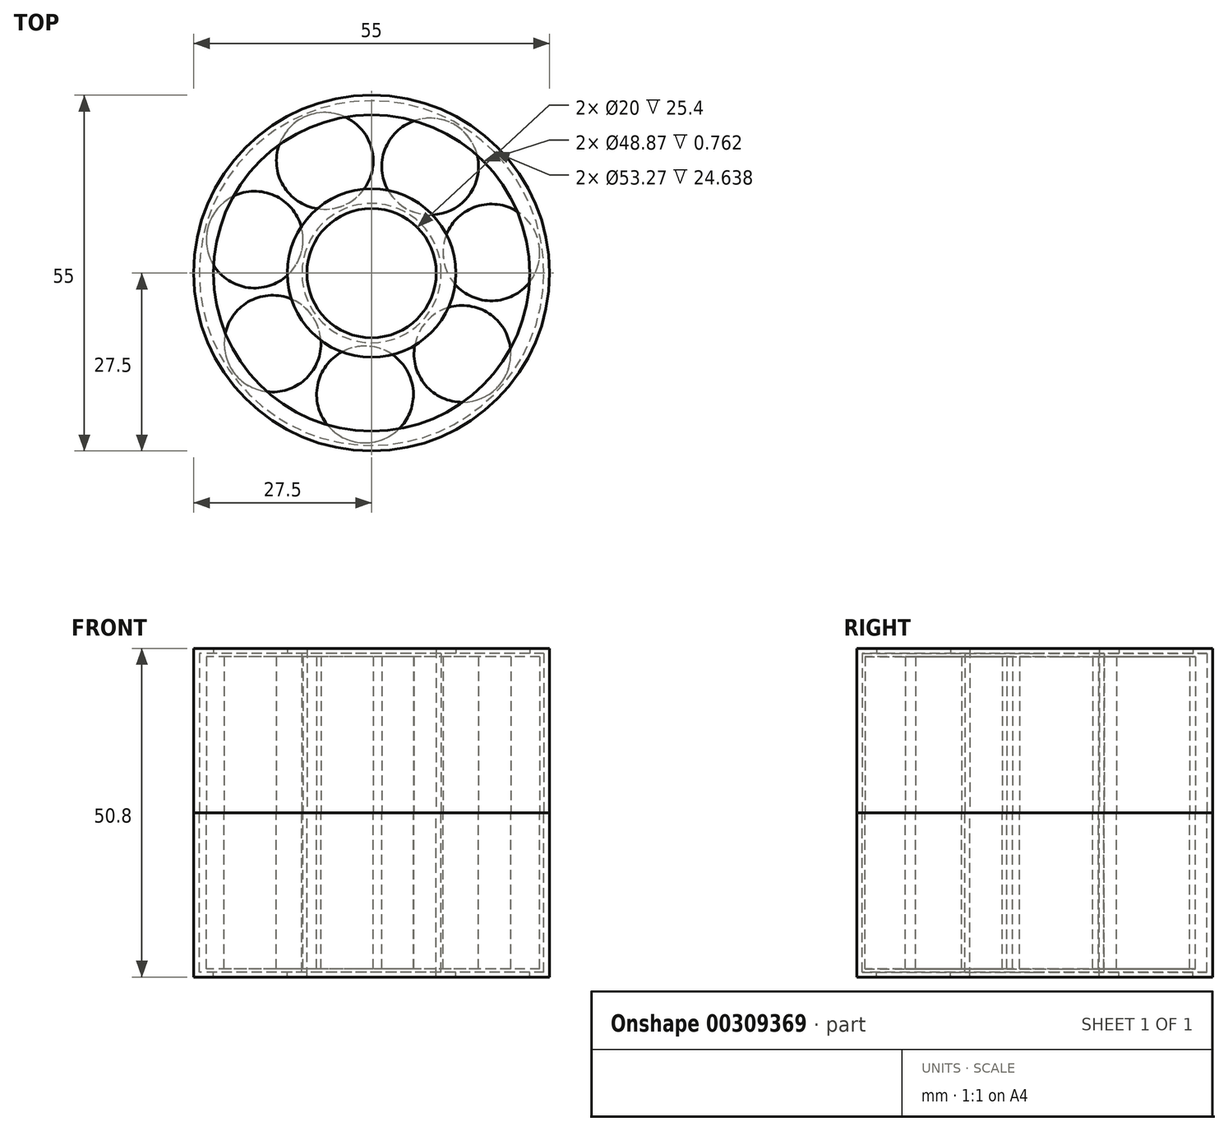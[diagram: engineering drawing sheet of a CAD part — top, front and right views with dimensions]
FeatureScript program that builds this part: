
annotation { "Feature Type Name" : "Feature", "Feature Type Description" : "" }
export const myFeature = defineFeature(function(context is Context, id is Id, definition is map)
    precondition{}
    {
        {
            var Q0;
            Q0=qCreatedBy(makeId("Top.planeOp"),FACE);
            var sketch = newSketch(context, id + "F0", { "sketchPlane" : qUnion([Q0])});
            skCircle(sketch, "E0", {"center": v(0, 0) * mm, "radius": 10 * mm});
            skCircle(sketch, "E1", {"center": v(0, 0) * mm, "radius": 27.5 * mm});
            skCircle(sketch, "E2", {"center": v(0, 0) * mm, "radius": 13.02 * mm});
            skCircle(sketch, "E3", {"center": v(0, 0) * mm, "radius": 24.43 * mm});
            skCircle(sketch, "E4", {"center": v(0, 0) * mm, "radius": 18.75 * mm, "construction": true});
            skCircle(sketch, "E5", {"center": v(0, 0) * mm, "radius": 10.76 * mm});
            skCircle(sketch, "E6", {"center": v(0, 0) * mm, "radius": 26.63 * mm});
            skCircle(sketch, "E7.cCircle", {"center": v(0, 0) * mm, "radius": 16.93 * mm, "construction": true});
            skLineSegment(sketch, "E7.0", {"start": v(9.05, 16.47) * mm, "end": v(18.52, 3.19) * mm});
            skLineSegment(sketch, "E7.1", {"start": v(18.52, 3.19) * mm, "end": v(14.04, -12.5) * mm});
            skLineSegment(sketch, "E7.2", {"start": v(14.04, -12.5) * mm, "end": v(-1.01, -18.76) * mm});
            skLineSegment(sketch, "E7.3", {"start": v(-1.01, -18.76) * mm, "end": v(-15.3, -10.9) * mm});
            skLineSegment(sketch, "E7.4", {"start": v(-15.3, -10.9) * mm, "end": v(-18.07, 5.16) * mm});
            skLineSegment(sketch, "E7.5", {"start": v(-18.07, 5.16) * mm, "end": v(-7.23, 17.34) * mm});
            skLineSegment(sketch, "E7.6", {"start": v(-7.23, 17.34) * mm, "end": v(9.05, 16.47) * mm});
            skPoint(sketch, "E7.0.midPoint", {"position": v(13.79, 9.83) * mm});
            skCircle(sketch, "E8", {"center": v(-7.23, 17.34) * mm, "radius": 7.48 * mm});
            skCircle(sketch, "E9", {"center": v(9.05, 16.47) * mm, "radius": 7.48 * mm});
            skCircle(sketch, "E10", {"center": v(18.52, 3.19) * mm, "radius": 7.48 * mm});
            skCircle(sketch, "E11", {"center": v(14.04, -12.5) * mm, "radius": 7.48 * mm});
            skCircle(sketch, "E12", {"center": v(-1.01, -18.76) * mm, "radius": 7.48 * mm});
            skCircle(sketch, "E13", {"center": v(-15.3, -10.9) * mm, "radius": 7.48 * mm});
            skCircle(sketch, "E14", {"center": v(-18.07, 5.16) * mm, "radius": 7.48 * mm});
            skSolve(sketch);
        }
        {
            var Q0;
            Q0 = qSketchRegion(id + "F0", true);
            var Q1;
            Q1=makeQuery(id+"F0.imprint","IMPRINT",FACE,{"disambiguationData":[TD([[makeQuery(id+"F0.imprint","IMPRINT",EDGE,{"derivedFrom":sQuery(id+"F0.wireOp",EDGE,"E0")}),-1.0]])]});
            var Q2;
            Q2=makeQuery(id+"F0.imprint","IMPRINT",FACE,{"disambiguationData":[TD([[makeQuery(id+"F0.imprint","IMPRINT",EDGE,{"derivedFrom":sQuery(id+"F0.wireOp",EDGE,"nIhnmfeC-0gWH-qgGF-FQwQ-DqKGUn8nxgKd")}),-1.0]])]});
            var Q3;
            Q3=makeQuery(id+"F0.imprint","IMPRINT",FACE,{"disambiguationData":[TD([[makeQuery(id+"F0.imprint","IMPRINT",EDGE,{"derivedFrom":sQuery(id+"F0.wireOp",EDGE,"kMlYBa3b-KAGz-d3cv-tEsV-yyaXbjt7PMGd")}),1.0]])]});
            var Q4;
            {var subQ0=sQuery(id+"F0.wireOp",EDGE,"E2");var subQ1=sQuery(id+"F0.wireOp",EDGE,"VeNGo6Cm-qSl3-L9k0-Q7Ts-Sp1q9LBLhO9i");var subQ2=makeQuery(id+"F0.imprint","INTERSECT",VERTEX,{"disambiguationData":[OD(0.0)],"derivedFrom":[subQ1,subQ0]});Q4=makeQuery(id+"F0.imprint","IMPRINT",FACE,{"disambiguationData":[TD([[makeQuery(id+"F0.imprint","IMPRINT",EDGE,{"disambiguationData":[TD([[subQ2,-1.0]])],"derivedFrom":subQ1}),1.0]])]});}
            var Q5;
            {var subQ0=sQuery(id+"F0.wireOp",EDGE,"E2");var subQ1=sQuery(id+"F0.wireOp",EDGE,"zqxHkr2o-9LMR-s23B-vHwf-xSVSSCzzs4RS");var subQ2=makeQuery(id+"F0.imprint","INTERSECT",VERTEX,{"disambiguationData":[OD(0.0)],"derivedFrom":[subQ1,subQ0]});Q5=makeQuery(id+"F0.imprint","IMPRINT",FACE,{"disambiguationData":[TD([[makeQuery(id+"F0.imprint","IMPRINT",EDGE,{"disambiguationData":[TD([[subQ2,1.0]])],"derivedFrom":subQ1}),1.0]])]});}
            var Q6;
            {var subQ0=sQuery(id+"F0.wireOp",EDGE,"E2");var subQ1=sQuery(id+"F0.wireOp",EDGE,"xxg3d6mS-jKbs-yPx6-TI2x-z0IN7hIOQDgV");var subQ2=makeQuery(id+"F0.imprint","INTERSECT",VERTEX,{"disambiguationData":[OD(0.0)],"derivedFrom":[subQ1,subQ0]});Q6=makeQuery(id+"F0.imprint","IMPRINT",FACE,{"disambiguationData":[TD([[makeQuery(id+"F0.imprint","IMPRINT",EDGE,{"disambiguationData":[TD([[subQ2,1.0]])],"derivedFrom":subQ1}),1.0]])]});}
            var Q7;
            {var subQ0=sQuery(id+"F0.wireOp",EDGE,"E2");var subQ1=sQuery(id+"F0.wireOp",EDGE,"EG8hidmS-nRKZ-wcGO-puJM-sy69pmvQp8kP");var subQ2=makeQuery(id+"F0.imprint","INTERSECT",VERTEX,{"disambiguationData":[OD(0.0)],"derivedFrom":[subQ1,subQ0]});Q7=makeQuery(id+"F0.imprint","IMPRINT",FACE,{"disambiguationData":[TD([[makeQuery(id+"F0.imprint","IMPRINT",EDGE,{"disambiguationData":[TD([[subQ2,-1.0]])],"derivedFrom":subQ1}),1.0]])]});}
            var Q8;
            {var subQ0=sQuery(id+"F0.wireOp",EDGE,"E2");var subQ1=sQuery(id+"F0.wireOp",EDGE,"lMHOxLXC-queE-13hP-3AmH-u1hImJZGGyEp");var subQ2=makeQuery(id+"F0.imprint","INTERSECT",VERTEX,{"disambiguationData":[OD(0.0)],"derivedFrom":[subQ1,subQ0]});Q8=makeQuery(id+"F0.imprint","IMPRINT",FACE,{"disambiguationData":[TD([[makeQuery(id+"F0.imprint","IMPRINT",EDGE,{"disambiguationData":[TD([[subQ2,-1.0]])],"derivedFrom":subQ1}),1.0]])]});}
            var Q9;
            {var subQ0=sQuery(id+"F0.wireOp",EDGE,"E2");var subQ1=sQuery(id+"F0.wireOp",EDGE,"Q5qxaiEa-uetU-TrzA-PZdv-cf9O0egGTCUz");var subQ2=makeQuery(id+"F0.imprint","INTERSECT",VERTEX,{"disambiguationData":[OD(0.0)],"derivedFrom":[subQ1,subQ0]});Q9=makeQuery(id+"F0.imprint","IMPRINT",FACE,{"disambiguationData":[TD([[makeQuery(id+"F0.imprint","IMPRINT",EDGE,{"disambiguationData":[TD([[subQ2,-1.0]])],"derivedFrom":subQ1}),1.0]])]});}
            var Q10;
            {var subQ0=sQuery(id+"F0.wireOp",EDGE,"np1IEidV-92wI-X2Ku-ilMX-xF02V59ttlWc");var subQ1=sQuery(id+"F0.wireOp",EDGE,"VeNGo6Cm-qSl3-L9k0-Q7Ts-Sp1q9LBLhO9i");var subQ2=makeQuery(id+"F0.imprint","INTERSECT",VERTEX,{"disambiguationData":[OD(0.0)],"derivedFrom":[subQ1,subQ0]});Q10=makeQuery(id+"F0.imprint","IMPRINT",FACE,{"disambiguationData":[TD([[makeQuery(id+"F0.imprint","IMPRINT",EDGE,{"disambiguationData":[TD([[subQ2,1.0]])],"derivedFrom":subQ1}),1.0]])]});}
            var Q11;
            {var subQ0=sQuery(id+"F0.wireOp",EDGE,"np1IEidV-92wI-X2Ku-ilMX-xF02V59ttlWc");var subQ1=sQuery(id+"F0.wireOp",EDGE,"Q5qxaiEa-uetU-TrzA-PZdv-cf9O0egGTCUz");var subQ2=makeQuery(id+"F0.imprint","INTERSECT",VERTEX,{"disambiguationData":[OD(0.0)],"derivedFrom":[subQ1,subQ0]});Q11=makeQuery(id+"F0.imprint","IMPRINT",FACE,{"disambiguationData":[TD([[makeQuery(id+"F0.imprint","IMPRINT",EDGE,{"disambiguationData":[TD([[subQ2,1.0]])],"derivedFrom":subQ1}),1.0]])]});}
            var Q12;
            {var subQ0=sQuery(id+"F0.wireOp",EDGE,"np1IEidV-92wI-X2Ku-ilMX-xF02V59ttlWc");var subQ1=sQuery(id+"F0.wireOp",EDGE,"lMHOxLXC-queE-13hP-3AmH-u1hImJZGGyEp");var subQ2=makeQuery(id+"F0.imprint","INTERSECT",VERTEX,{"disambiguationData":[OD(0.0)],"derivedFrom":[subQ1,subQ0]});Q12=makeQuery(id+"F0.imprint","IMPRINT",FACE,{"disambiguationData":[TD([[makeQuery(id+"F0.imprint","IMPRINT",EDGE,{"disambiguationData":[TD([[subQ2,1.0]])],"derivedFrom":subQ1}),1.0]])]});}
            var Q13;
            {var subQ0=sQuery(id+"F0.wireOp",EDGE,"np1IEidV-92wI-X2Ku-ilMX-xF02V59ttlWc");var subQ1=sQuery(id+"F0.wireOp",EDGE,"EG8hidmS-nRKZ-wcGO-puJM-sy69pmvQp8kP");var subQ2=makeQuery(id+"F0.imprint","INTERSECT",VERTEX,{"disambiguationData":[OD(0.0)],"derivedFrom":[subQ1,subQ0]});Q13=makeQuery(id+"F0.imprint","IMPRINT",FACE,{"disambiguationData":[TD([[makeQuery(id+"F0.imprint","IMPRINT",EDGE,{"disambiguationData":[TD([[subQ2,-1.0]])],"derivedFrom":subQ1}),1.0]])]});}
            var Q14;
            {var subQ0=sQuery(id+"F0.wireOp",EDGE,"np1IEidV-92wI-X2Ku-ilMX-xF02V59ttlWc");var subQ1=sQuery(id+"F0.wireOp",EDGE,"xxg3d6mS-jKbs-yPx6-TI2x-z0IN7hIOQDgV");var subQ2=makeQuery(id+"F0.imprint","INTERSECT",VERTEX,{"disambiguationData":[OD(0.0)],"derivedFrom":[subQ1,subQ0]});Q14=makeQuery(id+"F0.imprint","IMPRINT",FACE,{"disambiguationData":[TD([[makeQuery(id+"F0.imprint","IMPRINT",EDGE,{"disambiguationData":[TD([[subQ2,-1.0]])],"derivedFrom":subQ1}),1.0]])]});}
            var Q15;
            {var subQ0=sQuery(id+"F0.wireOp",EDGE,"np1IEidV-92wI-X2Ku-ilMX-xF02V59ttlWc");var subQ1=sQuery(id+"F0.wireOp",EDGE,"zqxHkr2o-9LMR-s23B-vHwf-xSVSSCzzs4RS");var subQ2=makeQuery(id+"F0.imprint","INTERSECT",VERTEX,{"disambiguationData":[OD(0.0)],"derivedFrom":[subQ1,subQ0]});Q15=makeQuery(id+"F0.imprint","IMPRINT",FACE,{"disambiguationData":[TD([[makeQuery(id+"F0.imprint","IMPRINT",EDGE,{"disambiguationData":[TD([[subQ2,-1.0]])],"derivedFrom":subQ1}),1.0]])]});}
            var Q16;
            Q16=makeQuery(id+"F0.imprint","IMPRINT",FACE,{"disambiguationData":[TD([[makeQuery(id+"F0.imprint","IMPRINT",EDGE,{"derivedFrom":sQuery(id+"F0.wireOp",EDGE,"E6")}),1.0]])]});
            var Q17;
            {var subQ0=sQuery(id+"F0.wireOp",EDGE,"E9");var subQ1=sQuery(id+"F0.wireOp",EDGE,"E3");var subQ2=makeQuery(id+"F0.imprint","INTERSECT",VERTEX,{"disambiguationData":[OD(0.0)],"derivedFrom":[subQ1,subQ0]});Q17=makeQuery(id+"F0.imprint","IMPRINT",FACE,{"disambiguationData":[TD([[makeQuery(id+"F0.imprint","IMPRINT",EDGE,{"disambiguationData":[TD([[subQ2,-1.0]])],"derivedFrom":subQ1}),-1.0]])]});}
            var Q18;
            {var subQ0=sQuery(id+"F0.wireOp",EDGE,"E10");var subQ1=sQuery(id+"F0.wireOp",EDGE,"E3");var subQ2=makeQuery(id+"F0.imprint","INTERSECT",VERTEX,{"disambiguationData":[OD(0.0)],"derivedFrom":[subQ1,subQ0]});Q18=makeQuery(id+"F0.imprint","IMPRINT",FACE,{"disambiguationData":[TD([[makeQuery(id+"F0.imprint","IMPRINT",EDGE,{"disambiguationData":[TD([[subQ2,1.0]])],"derivedFrom":subQ1}),-1.0]])]});}
            var Q19;
            {var subQ0=sQuery(id+"F0.wireOp",EDGE,"E11");var subQ1=sQuery(id+"F0.wireOp",EDGE,"E3");var subQ2=makeQuery(id+"F0.imprint","INTERSECT",VERTEX,{"disambiguationData":[OD(0.0)],"derivedFrom":[subQ1,subQ0]});Q19=makeQuery(id+"F0.imprint","IMPRINT",FACE,{"disambiguationData":[TD([[makeQuery(id+"F0.imprint","IMPRINT",EDGE,{"disambiguationData":[TD([[subQ2,-1.0]])],"derivedFrom":subQ1}),-1.0]])]});}
            var Q20;
            {var subQ0=sQuery(id+"F0.wireOp",EDGE,"E12");var subQ1=sQuery(id+"F0.wireOp",EDGE,"E3");var subQ2=makeQuery(id+"F0.imprint","INTERSECT",VERTEX,{"disambiguationData":[OD(0.0)],"derivedFrom":[subQ1,subQ0]});Q20=makeQuery(id+"F0.imprint","IMPRINT",FACE,{"disambiguationData":[TD([[makeQuery(id+"F0.imprint","IMPRINT",EDGE,{"disambiguationData":[TD([[subQ2,-1.0]])],"derivedFrom":subQ1}),-1.0]])]});}
            var Q21;
            {var subQ0=sQuery(id+"F0.wireOp",EDGE,"E13");var subQ1=sQuery(id+"F0.wireOp",EDGE,"E3");var subQ2=makeQuery(id+"F0.imprint","INTERSECT",VERTEX,{"disambiguationData":[OD(0.0)],"derivedFrom":[subQ1,subQ0]});Q21=makeQuery(id+"F0.imprint","IMPRINT",FACE,{"disambiguationData":[TD([[makeQuery(id+"F0.imprint","IMPRINT",EDGE,{"disambiguationData":[TD([[subQ2,-1.0]])],"derivedFrom":subQ1}),-1.0]])]});}
            var Q22;
            {var subQ0=sQuery(id+"F0.wireOp",EDGE,"E14");var subQ1=sQuery(id+"F0.wireOp",EDGE,"E3");var subQ2=makeQuery(id+"F0.imprint","INTERSECT",VERTEX,{"disambiguationData":[OD(0.0)],"derivedFrom":[subQ1,subQ0]});Q22=makeQuery(id+"F0.imprint","IMPRINT",FACE,{"disambiguationData":[TD([[makeQuery(id+"F0.imprint","IMPRINT",EDGE,{"disambiguationData":[TD([[subQ2,-1.0]])],"derivedFrom":subQ1}),-1.0]])]});}
            var Q23;
            {var subQ0=sQuery(id+"F0.wireOp",EDGE,"E8");var subQ1=sQuery(id+"F0.wireOp",EDGE,"E3");var subQ2=makeQuery(id+"F0.imprint","INTERSECT",VERTEX,{"disambiguationData":[OD(0.0)],"derivedFrom":[subQ1,subQ0]});Q23=makeQuery(id+"F0.imprint","IMPRINT",FACE,{"disambiguationData":[TD([[makeQuery(id+"F0.imprint","IMPRINT",EDGE,{"disambiguationData":[TD([[subQ2,-1.0]])],"derivedFrom":subQ1}),-1.0]])]});}
            var Q24;
            Q24=makeQuery(id+"F0.imprint","IMPRINT",FACE,{"disambiguationData":[TD([[makeQuery(id+"F0.imprint","IMPRINT",EDGE,{"derivedFrom":sQuery(id+"F0.wireOp",EDGE,"E5")}),-1.0]])]});
            var Q25;
            {var subQ0=sQuery(id+"F0.wireOp",EDGE,"E8");var subQ1=sQuery(id+"F0.wireOp",EDGE,"E2");var subQ2=makeQuery(id+"F0.imprint","INTERSECT",VERTEX,{"disambiguationData":[OD(0.0)],"derivedFrom":[subQ1,subQ0]});Q25=makeQuery(id+"F0.imprint","IMPRINT",FACE,{"disambiguationData":[TD([[makeQuery(id+"F0.imprint","IMPRINT",EDGE,{"disambiguationData":[TD([[subQ2,-1.0]])],"derivedFrom":subQ1}),1.0]])]});}
            var Q26;
            {var subQ0=sQuery(id+"F0.wireOp",EDGE,"E9");var subQ1=sQuery(id+"F0.wireOp",EDGE,"E2");var subQ2=makeQuery(id+"F0.imprint","INTERSECT",VERTEX,{"disambiguationData":[OD(0.0)],"derivedFrom":[subQ1,subQ0]});Q26=makeQuery(id+"F0.imprint","IMPRINT",FACE,{"disambiguationData":[TD([[makeQuery(id+"F0.imprint","IMPRINT",EDGE,{"disambiguationData":[TD([[subQ2,-1.0]])],"derivedFrom":subQ1}),1.0]])]});}
            var Q27;
            {var subQ0=sQuery(id+"F0.wireOp",EDGE,"E10");var subQ1=sQuery(id+"F0.wireOp",EDGE,"E2");var subQ2=makeQuery(id+"F0.imprint","INTERSECT",VERTEX,{"disambiguationData":[OD(0.0)],"derivedFrom":[subQ1,subQ0]});Q27=makeQuery(id+"F0.imprint","IMPRINT",FACE,{"disambiguationData":[TD([[makeQuery(id+"F0.imprint","IMPRINT",EDGE,{"disambiguationData":[TD([[subQ2,1.0]])],"derivedFrom":subQ1}),1.0]])]});}
            var Q28;
            {var subQ0=sQuery(id+"F0.wireOp",EDGE,"E11");var subQ1=sQuery(id+"F0.wireOp",EDGE,"E2");var subQ2=makeQuery(id+"F0.imprint","INTERSECT",VERTEX,{"disambiguationData":[OD(0.0)],"derivedFrom":[subQ1,subQ0]});Q28=makeQuery(id+"F0.imprint","IMPRINT",FACE,{"disambiguationData":[TD([[makeQuery(id+"F0.imprint","IMPRINT",EDGE,{"disambiguationData":[TD([[subQ2,-1.0]])],"derivedFrom":subQ1}),1.0]])]});}
            var Q29;
            {var subQ0=sQuery(id+"F0.wireOp",EDGE,"E12");var subQ1=sQuery(id+"F0.wireOp",EDGE,"E2");var subQ2=makeQuery(id+"F0.imprint","INTERSECT",VERTEX,{"disambiguationData":[OD(0.0)],"derivedFrom":[subQ1,subQ0]});Q29=makeQuery(id+"F0.imprint","IMPRINT",FACE,{"disambiguationData":[TD([[makeQuery(id+"F0.imprint","IMPRINT",EDGE,{"disambiguationData":[TD([[subQ2,-1.0]])],"derivedFrom":subQ1}),1.0]])]});}
            var Q30;
            {var subQ0=sQuery(id+"F0.wireOp",EDGE,"E13");var subQ1=sQuery(id+"F0.wireOp",EDGE,"E2");var subQ2=makeQuery(id+"F0.imprint","INTERSECT",VERTEX,{"disambiguationData":[OD(0.0)],"derivedFrom":[subQ1,subQ0]});Q30=makeQuery(id+"F0.imprint","IMPRINT",FACE,{"disambiguationData":[TD([[makeQuery(id+"F0.imprint","IMPRINT",EDGE,{"disambiguationData":[TD([[subQ2,-1.0]])],"derivedFrom":subQ1}),1.0]])]});}
            var Q31;
            {var subQ0=sQuery(id+"F0.wireOp",EDGE,"E14");var subQ1=sQuery(id+"F0.wireOp",EDGE,"E2");var subQ2=makeQuery(id+"F0.imprint","INTERSECT",VERTEX,{"disambiguationData":[OD(0.0)],"derivedFrom":[subQ1,subQ0]});Q31=makeQuery(id+"F0.imprint","IMPRINT",FACE,{"disambiguationData":[TD([[makeQuery(id+"F0.imprint","IMPRINT",EDGE,{"disambiguationData":[TD([[subQ2,-1.0]])],"derivedFrom":subQ1}),1.0]])]});}
            extrude(context, id + "F1", {"entities" : qUnion([Q0, Q1, Q2, Q3, Q4, Q5, Q6, Q7, Q8, Q9, Q10, Q11, Q12, Q13, Q14, Q15, Q16, Q17, Q18, Q19, Q20, Q21, Q22, Q23, Q24, Q25, Q26, Q27, Q28, Q29, Q30, Q31]), "depth" : 25.4 * mm});
        }
        {
            var Q0;
            Q0=makeQuery(id+"F0.imprint","IMPRINT",FACE,{"disambiguationData":[TD([[makeQuery(id+"F0.imprint","IMPRINT",EDGE,{"derivedFrom":sQuery(id+"F0.wireOp",EDGE,"E6")}),1.0]])]});
            var Q1;
            {var subQ0=sQuery(id+"F0.wireOp",EDGE,"E14");var subQ1=sQuery(id+"F0.wireOp",EDGE,"E3");var subQ2=makeQuery(id+"F0.imprint","INTERSECT",VERTEX,{"disambiguationData":[OD(0.0)],"derivedFrom":[subQ1,subQ0]});Q1=makeQuery(id+"F0.imprint","IMPRINT",FACE,{"disambiguationData":[TD([[makeQuery(id+"F0.imprint","IMPRINT",EDGE,{"disambiguationData":[TD([[subQ2,-1.0]])],"derivedFrom":subQ1}),-1.0]])]});}
            var Q2;
            {var subQ0=sQuery(id+"F0.wireOp",EDGE,"E13");var subQ1=sQuery(id+"F0.wireOp",EDGE,"E3");var subQ2=makeQuery(id+"F0.imprint","INTERSECT",VERTEX,{"disambiguationData":[OD(0.0)],"derivedFrom":[subQ1,subQ0]});Q2=makeQuery(id+"F0.imprint","IMPRINT",FACE,{"disambiguationData":[TD([[makeQuery(id+"F0.imprint","IMPRINT",EDGE,{"disambiguationData":[TD([[subQ2,-1.0]])],"derivedFrom":subQ1}),-1.0]])]});}
            var Q3;
            {var subQ0=sQuery(id+"F0.wireOp",EDGE,"E12");var subQ1=sQuery(id+"F0.wireOp",EDGE,"E3");var subQ2=makeQuery(id+"F0.imprint","INTERSECT",VERTEX,{"disambiguationData":[OD(0.0)],"derivedFrom":[subQ1,subQ0]});Q3=makeQuery(id+"F0.imprint","IMPRINT",FACE,{"disambiguationData":[TD([[makeQuery(id+"F0.imprint","IMPRINT",EDGE,{"disambiguationData":[TD([[subQ2,-1.0]])],"derivedFrom":subQ1}),-1.0]])]});}
            var Q4;
            {var subQ0=sQuery(id+"F0.wireOp",EDGE,"E11");var subQ1=sQuery(id+"F0.wireOp",EDGE,"E3");var subQ2=makeQuery(id+"F0.imprint","INTERSECT",VERTEX,{"disambiguationData":[OD(0.0)],"derivedFrom":[subQ1,subQ0]});Q4=makeQuery(id+"F0.imprint","IMPRINT",FACE,{"disambiguationData":[TD([[makeQuery(id+"F0.imprint","IMPRINT",EDGE,{"disambiguationData":[TD([[subQ2,-1.0]])],"derivedFrom":subQ1}),-1.0]])]});}
            var Q5;
            {var subQ0=sQuery(id+"F0.wireOp",EDGE,"E10");var subQ1=sQuery(id+"F0.wireOp",EDGE,"E3");var subQ2=makeQuery(id+"F0.imprint","INTERSECT",VERTEX,{"disambiguationData":[OD(0.0)],"derivedFrom":[subQ1,subQ0]});Q5=makeQuery(id+"F0.imprint","IMPRINT",FACE,{"disambiguationData":[TD([[makeQuery(id+"F0.imprint","IMPRINT",EDGE,{"disambiguationData":[TD([[subQ2,1.0]])],"derivedFrom":subQ1}),-1.0]])]});}
            var Q6;
            {var subQ0=sQuery(id+"F0.wireOp",EDGE,"E9");var subQ1=sQuery(id+"F0.wireOp",EDGE,"E3");var subQ2=makeQuery(id+"F0.imprint","INTERSECT",VERTEX,{"disambiguationData":[OD(0.0)],"derivedFrom":[subQ1,subQ0]});Q6=makeQuery(id+"F0.imprint","IMPRINT",FACE,{"disambiguationData":[TD([[makeQuery(id+"F0.imprint","IMPRINT",EDGE,{"disambiguationData":[TD([[subQ2,-1.0]])],"derivedFrom":subQ1}),-1.0]])]});}
            var Q7;
            {var subQ0=sQuery(id+"F0.wireOp",EDGE,"E8");var subQ1=sQuery(id+"F0.wireOp",EDGE,"E3");var subQ2=makeQuery(id+"F0.imprint","INTERSECT",VERTEX,{"disambiguationData":[OD(0.0)],"derivedFrom":[subQ1,subQ0]});Q7=makeQuery(id+"F0.imprint","IMPRINT",FACE,{"disambiguationData":[TD([[makeQuery(id+"F0.imprint","IMPRINT",EDGE,{"disambiguationData":[TD([[subQ2,-1.0]])],"derivedFrom":subQ1}),-1.0]])]});}
            var Q8;
            Q8=makeQuery(id+"F0.imprint","IMPRINT",FACE,{"disambiguationData":[TD([[makeQuery(id+"F0.imprint","IMPRINT",EDGE,{"derivedFrom":sQuery(id+"F0.wireOp",EDGE,"E5")}),-1.0]])]});
            var Q9;
            {var subQ0=sQuery(id+"F0.wireOp",EDGE,"E9");var subQ1=sQuery(id+"F0.wireOp",EDGE,"E2");var subQ2=makeQuery(id+"F0.imprint","INTERSECT",VERTEX,{"disambiguationData":[OD(0.0)],"derivedFrom":[subQ1,subQ0]});Q9=makeQuery(id+"F0.imprint","IMPRINT",FACE,{"disambiguationData":[TD([[makeQuery(id+"F0.imprint","IMPRINT",EDGE,{"disambiguationData":[TD([[subQ2,-1.0]])],"derivedFrom":subQ1}),1.0]])]});}
            var Q10;
            {var subQ0=sQuery(id+"F0.wireOp",EDGE,"E8");var subQ1=sQuery(id+"F0.wireOp",EDGE,"E2");var subQ2=makeQuery(id+"F0.imprint","INTERSECT",VERTEX,{"disambiguationData":[OD(0.0)],"derivedFrom":[subQ1,subQ0]});Q10=makeQuery(id+"F0.imprint","IMPRINT",FACE,{"disambiguationData":[TD([[makeQuery(id+"F0.imprint","IMPRINT",EDGE,{"disambiguationData":[TD([[subQ2,-1.0]])],"derivedFrom":subQ1}),1.0]])]});}
            var Q11;
            {var subQ0=sQuery(id+"F0.wireOp",EDGE,"E10");var subQ1=sQuery(id+"F0.wireOp",EDGE,"E2");var subQ2=makeQuery(id+"F0.imprint","INTERSECT",VERTEX,{"disambiguationData":[OD(0.0)],"derivedFrom":[subQ1,subQ0]});Q11=makeQuery(id+"F0.imprint","IMPRINT",FACE,{"disambiguationData":[TD([[makeQuery(id+"F0.imprint","IMPRINT",EDGE,{"disambiguationData":[TD([[subQ2,1.0]])],"derivedFrom":subQ1}),1.0]])]});}
            var Q12;
            {var subQ0=sQuery(id+"F0.wireOp",EDGE,"E11");var subQ1=sQuery(id+"F0.wireOp",EDGE,"E2");var subQ2=makeQuery(id+"F0.imprint","INTERSECT",VERTEX,{"disambiguationData":[OD(0.0)],"derivedFrom":[subQ1,subQ0]});Q12=makeQuery(id+"F0.imprint","IMPRINT",FACE,{"disambiguationData":[TD([[makeQuery(id+"F0.imprint","IMPRINT",EDGE,{"disambiguationData":[TD([[subQ2,-1.0]])],"derivedFrom":subQ1}),1.0]])]});}
            var Q13;
            {var subQ0=sQuery(id+"F0.wireOp",EDGE,"E12");var subQ1=sQuery(id+"F0.wireOp",EDGE,"E2");var subQ2=makeQuery(id+"F0.imprint","INTERSECT",VERTEX,{"disambiguationData":[OD(0.0)],"derivedFrom":[subQ1,subQ0]});Q13=makeQuery(id+"F0.imprint","IMPRINT",FACE,{"disambiguationData":[TD([[makeQuery(id+"F0.imprint","IMPRINT",EDGE,{"disambiguationData":[TD([[subQ2,-1.0]])],"derivedFrom":subQ1}),1.0]])]});}
            var Q14;
            {var subQ0=sQuery(id+"F0.wireOp",EDGE,"E13");var subQ1=sQuery(id+"F0.wireOp",EDGE,"E2");var subQ2=makeQuery(id+"F0.imprint","INTERSECT",VERTEX,{"disambiguationData":[OD(0.0)],"derivedFrom":[subQ1,subQ0]});Q14=makeQuery(id+"F0.imprint","IMPRINT",FACE,{"disambiguationData":[TD([[makeQuery(id+"F0.imprint","IMPRINT",EDGE,{"disambiguationData":[TD([[subQ2,-1.0]])],"derivedFrom":subQ1}),1.0]])]});}
            var Q15;
            {var subQ0=sQuery(id+"F0.wireOp",EDGE,"E14");var subQ1=sQuery(id+"F0.wireOp",EDGE,"E2");var subQ2=makeQuery(id+"F0.imprint","INTERSECT",VERTEX,{"disambiguationData":[OD(0.0)],"derivedFrom":[subQ1,subQ0]});Q15=makeQuery(id+"F0.imprint","IMPRINT",FACE,{"disambiguationData":[TD([[makeQuery(id+"F0.imprint","IMPRINT",EDGE,{"disambiguationData":[TD([[subQ2,-1.0]])],"derivedFrom":subQ1}),1.0]])]});}
            extrude(context, id + "F2", {"entities" : qUnion([Q0, Q1, Q2, Q3, Q4, Q5, Q6, Q7, Q8, Q9, Q10, Q11, Q12, Q13, Q14, Q15]), "operationType" : NewBodyOperationType.REMOVE, "depth" : 24.64 * mm});
        }
        {
            var Q0;
            {var subQ0=sQuery(id+"F0.wireOp",EDGE,"E9");var subQ1=sQuery(id+"F0.wireOp",EDGE,"E3");var subQ2=makeQuery(id+"F0.imprint","INTERSECT",VERTEX,{"disambiguationData":[OD(0.0)],"derivedFrom":[subQ1,subQ0]});Q0=makeQuery(id+"F0.imprint","IMPRINT",FACE,{"disambiguationData":[TD([[makeQuery(id+"F0.imprint","IMPRINT",EDGE,{"disambiguationData":[TD([[subQ2,-1.0]])],"derivedFrom":subQ1}),-1.0]])]});}
            var Q1;
            {var subQ0=sQuery(id+"F0.wireOp",EDGE,"E9");var subQ1=sQuery(id+"F0.wireOp",EDGE,"E3");var subQ8=makeQuery(id+"F0.imprint","INTERSECT",VERTEX,{"disambiguationData":[OD(0.0)],"derivedFrom":[subQ1,subQ0]});Q1=makeQuery(id+"F0.imprint","IMPRINT",FACE,{"disambiguationData":[TD([[makeQuery(id+"F0.imprint","IMPRINT",EDGE,{"disambiguationData":[TD([[subQ8,-1.0]])],"derivedFrom":subQ1}),1.0]])]});}
            var Q2;
            {var subQ0=sQuery(id+"F0.wireOp",EDGE,"E9");var subQ1=sQuery(id+"F0.wireOp",EDGE,"E2");var subQ7=makeQuery(id+"F0.imprint","INTERSECT",VERTEX,{"disambiguationData":[OD(0.0)],"derivedFrom":[subQ1,subQ0]});Q2=makeQuery(id+"F0.imprint","IMPRINT",FACE,{"disambiguationData":[TD([[makeQuery(id+"F0.imprint","IMPRINT",EDGE,{"disambiguationData":[TD([[subQ7,-1.0]])],"derivedFrom":subQ1}),-1.0]])]});}
            var Q3;
            {var subQ0=sQuery(id+"F0.wireOp",EDGE,"E8");var subQ1=sQuery(id+"F0.wireOp",EDGE,"E3");var subQ2=makeQuery(id+"F0.imprint","INTERSECT",VERTEX,{"disambiguationData":[OD(0.0)],"derivedFrom":[subQ1,subQ0]});Q3=makeQuery(id+"F0.imprint","IMPRINT",FACE,{"disambiguationData":[TD([[makeQuery(id+"F0.imprint","IMPRINT",EDGE,{"disambiguationData":[TD([[subQ2,-1.0]])],"derivedFrom":subQ1}),-1.0]])]});}
            var Q4;
            {var subQ3=sQuery(id+"F0.wireOp",EDGE,"E8");var subQ5=sQuery(id+"F0.wireOp",EDGE,"E3");var subQ8=makeQuery(id+"F0.imprint","INTERSECT",VERTEX,{"disambiguationData":[OD(0.0)],"derivedFrom":[subQ5,subQ3]});Q4=makeQuery(id+"F0.imprint","IMPRINT",FACE,{"disambiguationData":[TD([[makeQuery(id+"F0.imprint","IMPRINT",EDGE,{"disambiguationData":[TD([[subQ8,-1.0]])],"derivedFrom":subQ5}),1.0]])]});}
            var Q5;
            {var subQ3=sQuery(id+"F0.wireOp",EDGE,"E8");var subQ5=sQuery(id+"F0.wireOp",EDGE,"E2");var subQ6=makeQuery(id+"F0.imprint","INTERSECT",VERTEX,{"disambiguationData":[OD(0.0)],"derivedFrom":[subQ5,subQ3]});Q5=makeQuery(id+"F0.imprint","IMPRINT",FACE,{"disambiguationData":[TD([[makeQuery(id+"F0.imprint","IMPRINT",EDGE,{"disambiguationData":[TD([[subQ6,-1.0]])],"derivedFrom":subQ5}),-1.0]])]});}
            var Q6;
            {var subQ0=sQuery(id+"F0.wireOp",EDGE,"E14");var subQ1=sQuery(id+"F0.wireOp",EDGE,"E3");var subQ2=makeQuery(id+"F0.imprint","INTERSECT",VERTEX,{"disambiguationData":[OD(0.0)],"derivedFrom":[subQ1,subQ0]});Q6=makeQuery(id+"F0.imprint","IMPRINT",FACE,{"disambiguationData":[TD([[makeQuery(id+"F0.imprint","IMPRINT",EDGE,{"disambiguationData":[TD([[subQ2,-1.0]])],"derivedFrom":subQ1}),1.0]])]});}
            var Q7;
            {var subQ0=sQuery(id+"F0.wireOp",EDGE,"E14");var subQ1=sQuery(id+"F0.wireOp",EDGE,"E3");var subQ2=makeQuery(id+"F0.imprint","INTERSECT",VERTEX,{"disambiguationData":[OD(0.0)],"derivedFrom":[subQ1,subQ0]});Q7=makeQuery(id+"F0.imprint","IMPRINT",FACE,{"disambiguationData":[TD([[makeQuery(id+"F0.imprint","IMPRINT",EDGE,{"disambiguationData":[TD([[subQ2,-1.0]])],"derivedFrom":subQ1}),-1.0]])]});}
            var Q8;
            {var subQ0=sQuery(id+"F0.wireOp",EDGE,"E14");var subQ1=sQuery(id+"F0.wireOp",EDGE,"E2");var subQ2=makeQuery(id+"F0.imprint","INTERSECT",VERTEX,{"disambiguationData":[OD(0.0)],"derivedFrom":[subQ1,subQ0]});Q8=makeQuery(id+"F0.imprint","IMPRINT",FACE,{"disambiguationData":[TD([[makeQuery(id+"F0.imprint","IMPRINT",EDGE,{"disambiguationData":[TD([[subQ2,-1.0]])],"derivedFrom":subQ1}),-1.0]])]});}
            var Q9;
            {var subQ3=sQuery(id+"F0.wireOp",EDGE,"E13");var subQ5=sQuery(id+"F0.wireOp",EDGE,"E2");var subQ6=makeQuery(id+"F0.imprint","INTERSECT",VERTEX,{"disambiguationData":[OD(0.0)],"derivedFrom":[subQ5,subQ3]});Q9=makeQuery(id+"F0.imprint","IMPRINT",FACE,{"disambiguationData":[TD([[makeQuery(id+"F0.imprint","IMPRINT",EDGE,{"disambiguationData":[TD([[subQ6,-1.0]])],"derivedFrom":subQ5}),-1.0]])]});}
            var Q10;
            {var subQ0=sQuery(id+"F0.wireOp",EDGE,"E13");var subQ1=sQuery(id+"F0.wireOp",EDGE,"E2");var subQ2=makeQuery(id+"F0.imprint","INTERSECT",VERTEX,{"disambiguationData":[OD(0.0)],"derivedFrom":[subQ1,subQ0]});Q10=makeQuery(id+"F0.imprint","IMPRINT",FACE,{"disambiguationData":[TD([[makeQuery(id+"F0.imprint","IMPRINT",EDGE,{"disambiguationData":[TD([[subQ2,-1.0]])],"derivedFrom":subQ1}),1.0]])]});}
            var Q11;
            {var subQ0=sQuery(id+"F0.wireOp",EDGE,"E13");var subQ1=sQuery(id+"F0.wireOp",EDGE,"E3");var subQ2=makeQuery(id+"F0.imprint","INTERSECT",VERTEX,{"disambiguationData":[OD(0.0)],"derivedFrom":[subQ1,subQ0]});Q11=makeQuery(id+"F0.imprint","IMPRINT",FACE,{"disambiguationData":[TD([[makeQuery(id+"F0.imprint","IMPRINT",EDGE,{"disambiguationData":[TD([[subQ2,-1.0]])],"derivedFrom":subQ1}),1.0]])]});}
            var Q12;
            {var subQ0=sQuery(id+"F0.wireOp",EDGE,"E13");var subQ1=sQuery(id+"F0.wireOp",EDGE,"E3");var subQ2=makeQuery(id+"F0.imprint","INTERSECT",VERTEX,{"disambiguationData":[OD(0.0)],"derivedFrom":[subQ1,subQ0]});Q12=makeQuery(id+"F0.imprint","IMPRINT",FACE,{"disambiguationData":[TD([[makeQuery(id+"F0.imprint","IMPRINT",EDGE,{"disambiguationData":[TD([[subQ2,-1.0]])],"derivedFrom":subQ1}),-1.0]])]});}
            var Q13;
            {var subQ0=sQuery(id+"F0.wireOp",EDGE,"E14");var subQ1=sQuery(id+"F0.wireOp",EDGE,"E2");var subQ2=makeQuery(id+"F0.imprint","INTERSECT",VERTEX,{"disambiguationData":[OD(0.0)],"derivedFrom":[subQ1,subQ0]});Q13=makeQuery(id+"F0.imprint","IMPRINT",FACE,{"disambiguationData":[TD([[makeQuery(id+"F0.imprint","IMPRINT",EDGE,{"disambiguationData":[TD([[subQ2,-1.0]])],"derivedFrom":subQ1}),1.0]])]});}
            var Q14;
            {var subQ0=sQuery(id+"F0.wireOp",EDGE,"E8");var subQ1=sQuery(id+"F0.wireOp",EDGE,"E2");var subQ2=makeQuery(id+"F0.imprint","INTERSECT",VERTEX,{"disambiguationData":[OD(0.0)],"derivedFrom":[subQ1,subQ0]});Q14=makeQuery(id+"F0.imprint","IMPRINT",FACE,{"disambiguationData":[TD([[makeQuery(id+"F0.imprint","IMPRINT",EDGE,{"disambiguationData":[TD([[subQ2,-1.0]])],"derivedFrom":subQ1}),1.0]])]});}
            var Q15;
            {var subQ0=sQuery(id+"F0.wireOp",EDGE,"E9");var subQ1=sQuery(id+"F0.wireOp",EDGE,"E2");var subQ2=makeQuery(id+"F0.imprint","INTERSECT",VERTEX,{"disambiguationData":[OD(0.0)],"derivedFrom":[subQ1,subQ0]});Q15=makeQuery(id+"F0.imprint","IMPRINT",FACE,{"disambiguationData":[TD([[makeQuery(id+"F0.imprint","IMPRINT",EDGE,{"disambiguationData":[TD([[subQ2,-1.0]])],"derivedFrom":subQ1}),1.0]])]});}
            var Q16;
            {var subQ0=sQuery(id+"F0.wireOp",EDGE,"E10");var subQ1=sQuery(id+"F0.wireOp",EDGE,"E2");var subQ2=makeQuery(id+"F0.imprint","INTERSECT",VERTEX,{"disambiguationData":[OD(0.0)],"derivedFrom":[subQ1,subQ0]});Q16=makeQuery(id+"F0.imprint","IMPRINT",FACE,{"disambiguationData":[TD([[makeQuery(id+"F0.imprint","IMPRINT",EDGE,{"disambiguationData":[TD([[subQ2,1.0]])],"derivedFrom":subQ1}),-1.0]])]});}
            var Q17;
            {var subQ0=sQuery(id+"F0.wireOp",EDGE,"E10");var subQ1=sQuery(id+"F0.wireOp",EDGE,"E3");var subQ2=makeQuery(id+"F0.imprint","INTERSECT",VERTEX,{"disambiguationData":[OD(0.0)],"derivedFrom":[subQ1,subQ0]});Q17=makeQuery(id+"F0.imprint","IMPRINT",FACE,{"disambiguationData":[TD([[makeQuery(id+"F0.imprint","IMPRINT",EDGE,{"disambiguationData":[TD([[subQ2,1.0]])],"derivedFrom":subQ1}),1.0]])]});}
            var Q18;
            {var subQ0=sQuery(id+"F0.wireOp",EDGE,"E10");var subQ1=sQuery(id+"F0.wireOp",EDGE,"E3");var subQ2=makeQuery(id+"F0.imprint","INTERSECT",VERTEX,{"disambiguationData":[OD(0.0)],"derivedFrom":[subQ1,subQ0]});Q18=makeQuery(id+"F0.imprint","IMPRINT",FACE,{"disambiguationData":[TD([[makeQuery(id+"F0.imprint","IMPRINT",EDGE,{"disambiguationData":[TD([[subQ2,1.0]])],"derivedFrom":subQ1}),-1.0]])]});}
            var Q19;
            {var subQ0=sQuery(id+"F0.wireOp",EDGE,"E10");var subQ1=sQuery(id+"F0.wireOp",EDGE,"E2");var subQ2=makeQuery(id+"F0.imprint","INTERSECT",VERTEX,{"disambiguationData":[OD(0.0)],"derivedFrom":[subQ1,subQ0]});Q19=makeQuery(id+"F0.imprint","IMPRINT",FACE,{"disambiguationData":[TD([[makeQuery(id+"F0.imprint","IMPRINT",EDGE,{"disambiguationData":[TD([[subQ2,1.0]])],"derivedFrom":subQ1}),1.0]])]});}
            var Q20;
            {var subQ0=sQuery(id+"F0.wireOp",EDGE,"E11");var subQ1=sQuery(id+"F0.wireOp",EDGE,"E2");var subQ2=makeQuery(id+"F0.imprint","INTERSECT",VERTEX,{"disambiguationData":[OD(0.0)],"derivedFrom":[subQ1,subQ0]});Q20=makeQuery(id+"F0.imprint","IMPRINT",FACE,{"disambiguationData":[TD([[makeQuery(id+"F0.imprint","IMPRINT",EDGE,{"disambiguationData":[TD([[subQ2,-1.0]])],"derivedFrom":subQ1}),1.0]])]});}
            var Q21;
            {var subQ0=sQuery(id+"F0.wireOp",EDGE,"E11");var subQ1=sQuery(id+"F0.wireOp",EDGE,"E2");var subQ8=makeQuery(id+"F0.imprint","INTERSECT",VERTEX,{"disambiguationData":[OD(0.0)],"derivedFrom":[subQ1,subQ0]});Q21=makeQuery(id+"F0.imprint","IMPRINT",FACE,{"disambiguationData":[TD([[makeQuery(id+"F0.imprint","IMPRINT",EDGE,{"disambiguationData":[TD([[subQ8,-1.0]])],"derivedFrom":subQ1}),-1.0]])]});}
            var Q22;
            {var subQ0=sQuery(id+"F0.wireOp",EDGE,"E11");var subQ1=sQuery(id+"F0.wireOp",EDGE,"E3");var subQ8=makeQuery(id+"F0.imprint","INTERSECT",VERTEX,{"disambiguationData":[OD(0.0)],"derivedFrom":[subQ1,subQ0]});Q22=makeQuery(id+"F0.imprint","IMPRINT",FACE,{"disambiguationData":[TD([[makeQuery(id+"F0.imprint","IMPRINT",EDGE,{"disambiguationData":[TD([[subQ8,-1.0]])],"derivedFrom":subQ1}),1.0]])]});}
            var Q23;
            {var subQ0=sQuery(id+"F0.wireOp",EDGE,"E11");var subQ1=sQuery(id+"F0.wireOp",EDGE,"E3");var subQ2=makeQuery(id+"F0.imprint","INTERSECT",VERTEX,{"disambiguationData":[OD(0.0)],"derivedFrom":[subQ1,subQ0]});Q23=makeQuery(id+"F0.imprint","IMPRINT",FACE,{"disambiguationData":[TD([[makeQuery(id+"F0.imprint","IMPRINT",EDGE,{"disambiguationData":[TD([[subQ2,-1.0]])],"derivedFrom":subQ1}),-1.0]])]});}
            var Q24;
            {var subQ0=sQuery(id+"F0.wireOp",EDGE,"E12");var subQ1=sQuery(id+"F0.wireOp",EDGE,"E2");var subQ2=makeQuery(id+"F0.imprint","INTERSECT",VERTEX,{"disambiguationData":[OD(0.0)],"derivedFrom":[subQ1,subQ0]});Q24=makeQuery(id+"F0.imprint","IMPRINT",FACE,{"disambiguationData":[TD([[makeQuery(id+"F0.imprint","IMPRINT",EDGE,{"disambiguationData":[TD([[subQ2,-1.0]])],"derivedFrom":subQ1}),1.0]])]});}
            var Q25;
            {var subQ0=sQuery(id+"F0.wireOp",EDGE,"E12");var subQ1=sQuery(id+"F0.wireOp",EDGE,"E2");var subQ5=makeQuery(id+"F0.imprint","INTERSECT",VERTEX,{"disambiguationData":[OD(0.0)],"derivedFrom":[subQ1,subQ0]});Q25=makeQuery(id+"F0.imprint","IMPRINT",FACE,{"disambiguationData":[TD([[makeQuery(id+"F0.imprint","IMPRINT",EDGE,{"disambiguationData":[TD([[subQ5,-1.0]])],"derivedFrom":subQ1}),-1.0]])]});}
            var Q26;
            {var subQ3=sQuery(id+"F0.wireOp",EDGE,"E12");var subQ5=sQuery(id+"F0.wireOp",EDGE,"E3");var subQ6=makeQuery(id+"F0.imprint","INTERSECT",VERTEX,{"disambiguationData":[OD(0.0)],"derivedFrom":[subQ5,subQ3]});Q26=makeQuery(id+"F0.imprint","IMPRINT",FACE,{"disambiguationData":[TD([[makeQuery(id+"F0.imprint","IMPRINT",EDGE,{"disambiguationData":[TD([[subQ6,-1.0]])],"derivedFrom":subQ5}),1.0]])]});}
            var Q27;
            {var subQ0=sQuery(id+"F0.wireOp",EDGE,"E12");var subQ1=sQuery(id+"F0.wireOp",EDGE,"E3");var subQ2=makeQuery(id+"F0.imprint","INTERSECT",VERTEX,{"disambiguationData":[OD(0.0)],"derivedFrom":[subQ1,subQ0]});Q27=makeQuery(id+"F0.imprint","IMPRINT",FACE,{"disambiguationData":[TD([[makeQuery(id+"F0.imprint","IMPRINT",EDGE,{"disambiguationData":[TD([[subQ2,-1.0]])],"derivedFrom":subQ1}),-1.0]])]});}
            extrude(context, id + "F3", {"entities" : qUnion([Q0, Q1, Q2, Q3, Q4, Q5, Q6, Q7, Q8, Q9, Q10, Q11, Q12, Q13, Q14, Q15, Q16, Q17, Q18, Q19, Q20, Q21, Q22, Q23, Q24, Q25, Q26, Q27]), "depth" : 24.13 * mm});
        }
        {
            var Q0;
            Q0=makeQuery(id+"F3.opExtrude","SWEPT_BODY",BODY,{"disambiguationData":[OSD([sQuery(id+"F0.wireOp",EDGE,"E13")])]});
            var Q1;
            Q1=makeQuery(id+"F3.opExtrude","SWEPT_BODY",BODY,{"disambiguationData":[OSD([sQuery(id+"F0.wireOp",EDGE,"E14")])]});
            var Q2;
            Q2=makeQuery(id+"F3.opExtrude","SWEPT_BODY",BODY,{"disambiguationData":[OSD([sQuery(id+"F0.wireOp",EDGE,"E8")])]});
            var Q3;
            Q3=makeQuery(id+"F3.opExtrude","SWEPT_BODY",BODY,{"disambiguationData":[OSD([sQuery(id+"F0.wireOp",EDGE,"E12")])]});
            var Q4;
            Q4=makeQuery(id+"F3.opExtrude","SWEPT_BODY",BODY,{"disambiguationData":[OSD([sQuery(id+"F0.wireOp",EDGE,"E11")])]});
            var Q5;
            Q5=makeQuery(id+"F3.opExtrude","SWEPT_BODY",BODY,{"disambiguationData":[OSD([sQuery(id+"F0.wireOp",EDGE,"E9")])]});
            var Q6;
            Q6=makeQuery(id+"F3.opExtrude","SWEPT_BODY",BODY,{"disambiguationData":[OSD([sQuery(id+"F0.wireOp",EDGE,"E10")])]});
            var Q7;
            Q7=makeQuery(id+"F1.opExtrude","SWEPT_BODY",BODY,{"disambiguationData":[OSD([sQuery(id+"F0.wireOp",EDGE,"E1"),sQuery(id+"F0.wireOp",EDGE,"E3")])]});
            var Q8;
            Q8=makeQuery(id+"F1.opExtrude","SWEPT_BODY",BODY,{"disambiguationData":[OSD([sQuery(id+"F0.wireOp",EDGE,"E0"),sQuery(id+"F0.wireOp",EDGE,"E2")])]});
            var Q9;
            Q9=qCreatedBy(makeId("Top.planeOp"),FACE);
            mirror(context, id + "F4", {"entities" : qUnion([Q0, Q1, Q2, Q3, Q4, Q5, Q6, Q7, Q8]), "mirrorPlane" : qUnion([Q9])});
        }
    });
